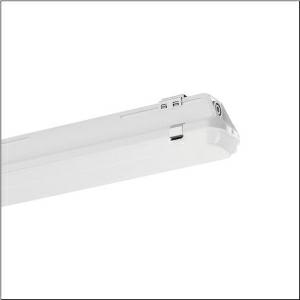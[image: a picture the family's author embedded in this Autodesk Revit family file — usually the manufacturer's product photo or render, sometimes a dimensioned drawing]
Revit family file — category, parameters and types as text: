
# Revit family: monsun_r__21_51fb107l420k005_9538
name_source: partatom
category: Lighting Fixtures
units: mm (PartAtom-declared; Revit-internal decimal feet)

## family parameters
Cut with Voids When Loaded = No
Host = Face
Light Source = No
Part Type = Normal
Room Calculation Point = No
Round Connector Dimension = Use Diameter
Shared = No

## types (1)
- Monsun® 21 (1 x LED, 2590 lm, 15.6 W, 4000K)
    Apparent Load = 16 VA
    CIE Flux Codes = 46 76 93 94 100
    Color Rendering = 80
    Color Temperature = 4000K
    Default Elevation = 1800 mm
    Description = Monsun® 21, damp-proof luminaire, chain hanger, primary optical cover: enclosure, of PMMA, light emission: direct distribution, primary light characteristic: symmetric, installation type: vertical mounting, horizontal mounting, surface-mounted, suspended mounting, LED, rated luminous flux: 2.590lm, luminous efficacy: 166lm/W, light colour: 840, colour temperature: 4000K, control gear: ON/OFF, with terminal, 3-pole, max. 2.5mm², through-wiring: 5x 2.5mm², mains connection: 220..240V, AC, 50/60Hz, rated input power: 16W, housing, of glass-fibre reinforced plastic, uncoated, bright grey, incl. chain hanger, length: 1.299mm, width: 90mm, height: 88mm, clip for enclosure, of stainless steel (V2A), ceiling mounting element, of stainless steel (V2A), chain hanger, of stainless steel (V2A), protection rating (complete): IP66, insulation class (complete): insulation class I (protective earthing), certification: CE, ENEC, VDE, UKCA, protection symbol: D, impact resistance: IK04, permissible operating ambient temperature: -25..+35°C, standard: EN 50419, EN 60598-2-1, corresponds to IFS (International Featured Standards) requirements for safety and quality in the food industry, for indoor or canopied outdoor use, no direct snow, no direct sun, no direct rain, LABS conformity tested according to VDMA 24364:2018-05, contact your sales advisor before using the luminaires in applications with unclear chemical exposure, large temperature fluctuations or condensation-forming humidity, packaging unit: 1 piece
    Height = 88 mm
    Lamp = 1 x LED
    Lamp Light Flux = 2590 lm
    Lamp Power = 15.6 W
    Lamp count = 1
    Length = 1299 mm
    Luminous efficacy = 166 lm/W
    Manufacturer = Siteco
    ModVariant = No
    Model = 51FB107L420K005
    Mounting Place = Ceiling
    Mounting Type = Surface mounted
    Number of Poles = 1
    OnlyDefault = Yes
    Power Factor = 1
    Product Name = Monsun® 21
    Product group = damp-proof luminaire
    ProductGroupID = 301
    Protection Class = Protection class I
    Protection Degree = IP 66
    RLX_Detail_Level = 1
    RLX_Emergency_Light_Flux = 0 lm
    RLX_Emergency_Type = 0
    RLX_Emergency_Type_DB = No
    RlxData = <blob elided: 89761 chars, md5=734e5c6c>
    Socket = socket
    Standby Power = 0 W
    System Light Flux = 2590 lm
    System Power = 16 W
    Type Comments = Product without accessories
    Type Image = l_1319656.jpg
    URL = http://relux.com
    VarID = ---
    Voltage = 0 V
    Weight = 0.00 kg
    Width = 90 mm

## geometry (parser evidence)
native form markers: Blend x4, Sweep x15
no freeform markers — native parametric forms only
